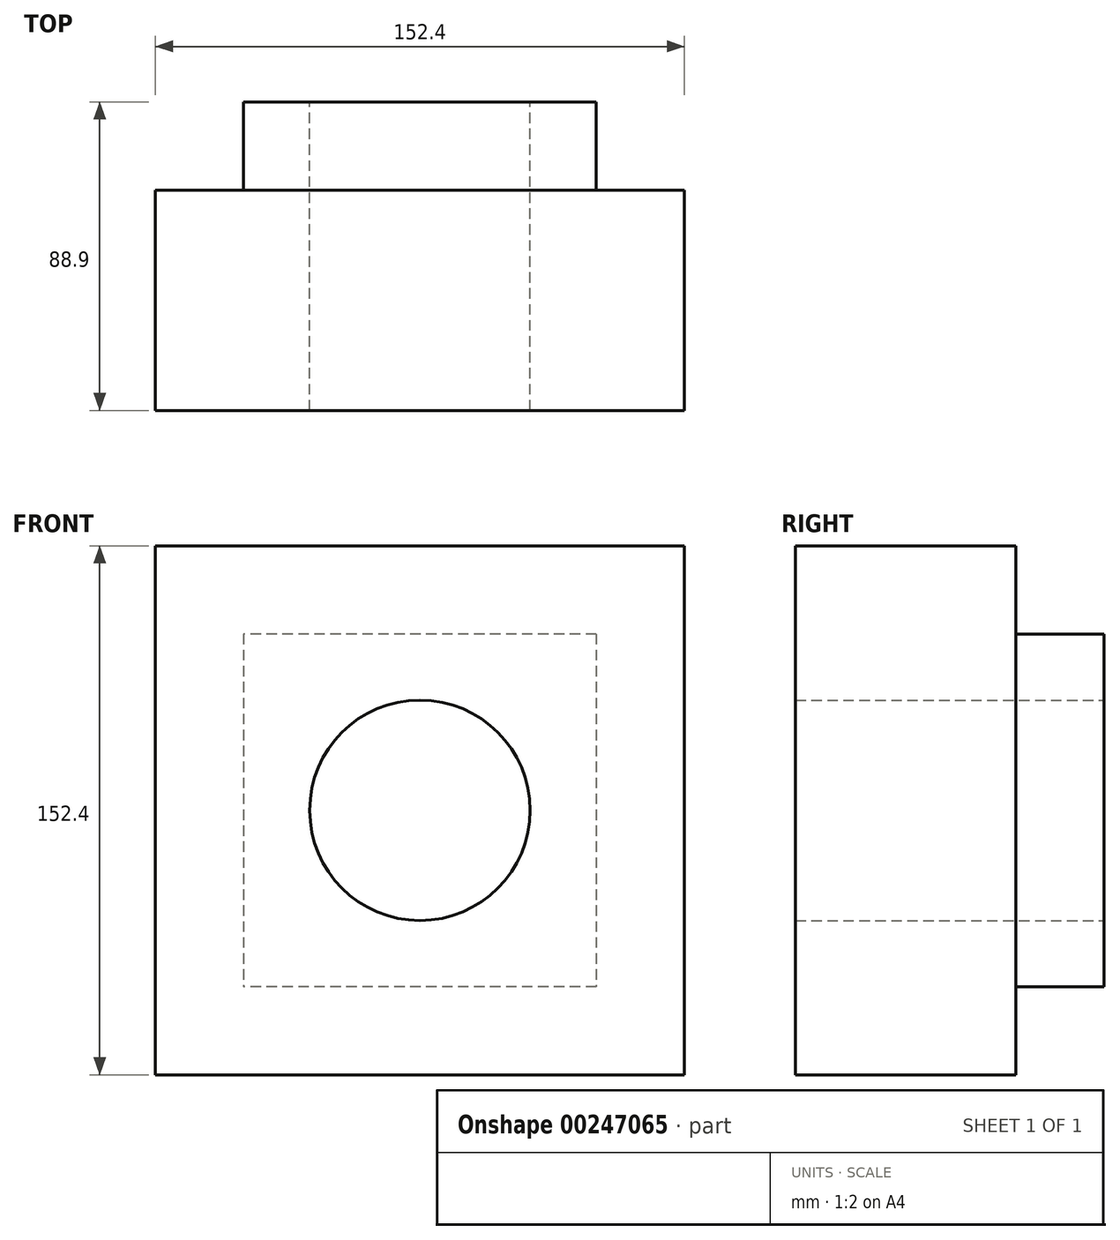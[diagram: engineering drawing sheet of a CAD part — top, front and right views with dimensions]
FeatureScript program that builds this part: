
annotation { "Feature Type Name" : "Feature", "Feature Type Description" : "" }
export const myFeature = defineFeature(function(context is Context, id is Id, definition is map)
    precondition{}
    {
        {
            var Q0;
            Q0=qCreatedBy(makeId("Front.planeOp"),FACE);
            var sketch = newSketch(context, id + "F0", { "sketchPlane" : qUnion([Q0])});
            skCircle(sketch, "E0", {"center": v(0, 0) * mm, "radius": 31.75 * mm});
            skLineSegment(sketch, "E1.bottom", {"start": v(76.2, 76.2) * mm, "end": v(-76.2, 76.2) * mm});
            skLineSegment(sketch, "E1.top", {"start": v(76.2, -76.2) * mm, "end": v(-76.2, -76.2) * mm});
            skLineSegment(sketch, "E1.left", {"start": v(76.2, 76.2) * mm, "end": v(76.2, -76.2) * mm});
            skLineSegment(sketch, "E1.right", {"start": v(-76.2, 76.2) * mm, "end": v(-76.2, -76.2) * mm});
            skLineSegment(sketch, "E2.bottom", {"start": v(50.8, 50.8) * mm, "end": v(-50.8, 50.8) * mm});
            skLineSegment(sketch, "E2.top", {"start": v(50.8, -50.8) * mm, "end": v(-50.8, -50.8) * mm});
            skLineSegment(sketch, "E2.left", {"start": v(50.8, 50.8) * mm, "end": v(50.8, -50.8) * mm});
            skLineSegment(sketch, "E2.right", {"start": v(-50.8, 50.8) * mm, "end": v(-50.8, -50.8) * mm});
            skSolve(sketch);
        }
        {
            var Q0;
            Q0=makeQuery(id+"F0.imprint","IMPRINT",FACE,{"disambiguationData":[TD([[makeQuery(id+"F0.imprint","IMPRINT",EDGE,{"derivedFrom":sQuery(id+"F0.wireOp",EDGE,"E1.bottom")}),1.0]])]});
            var Q1;
            Q1=makeQuery(id+"F0.imprint","IMPRINT",FACE,{"disambiguationData":[TD([[makeQuery(id+"F0.imprint","IMPRINT",EDGE,{"derivedFrom":sQuery(id+"F0.wireOp",EDGE,"E0")}),-1.0]])]});
            extrude(context, id + "F1", {"entities" : qUnion([Q0, Q1]), "depth" : 63.5 * mm});
        }
        {
            var Q0;
            Q0=makeQuery(id+"F0.imprint","IMPRINT",FACE,{"disambiguationData":[TD([[makeQuery(id+"F0.imprint","IMPRINT",EDGE,{"derivedFrom":sQuery(id+"F0.wireOp",EDGE,"E0")}),-1.0]])]});
            extrude(context, id + "F2", {"entities" : qUnion([Q0]), "operationType" : NewBodyOperationType.ADD, "oppositeDirection" : true, "depth" : 25.4 * mm});
        }
    });
